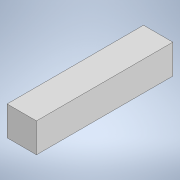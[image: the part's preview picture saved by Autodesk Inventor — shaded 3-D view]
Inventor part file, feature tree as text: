
AUTODESK INVENTOR PART (.ipt)
format: ipt  version: 2021 (Build 250183000, 183)  size: 96,768 bytes
history: native  units: in
note: dims shown in document units (in); Inventor stores cm internally (conversion verified against a paired STEP export)
features: extrude x1, sketch x1
ambient origin geometry x8: Origin, YZ Plane, XZ Plane, XY Plane, X Axis, Y Axis, Z Axis, Center Point
bodies: Solid1 (feature_tree)
feature tree (2):
  extrude  "Extrusion1"  Depth=7.75in
  sketch  "Sketch1"  dims[d5=36.0in d6=0.0in d7=7.75in d8=7.75in d9=0.625in d10=7.75in d11=0.625in]
